FCSTD DOCUMENT  (FreeCAD 0.19R24366 (Git))
Label: hulltest3
License: All rights reserved
LicenseURL: http://en.wikipedia.org/wiki/All_rights_reserved
objects: Sketcher::SketchObject×2, PartDesign::Body×1
note: 3 computed .brp shape members not serialized (recipe doc carries the construction recipe); baked Part::Feature solids carry a one-line shape summary decoded from their .brp

FEATURE [Sketcher::SketchObject] Sketch  label="HullOutline"
  FullyConstrained = false
  Placement = pos=(0,0,0) rot=(0.980944,0.137386,0.137386;1.59004rad)
  Support = -> [XZ_Plane001]
  sketch-geometry (9):
    g0: LineSegment StartX=0 StartY=4e-16 StartZ=0 EndX=160 EndY=3 EndZ=0
    g1: LineSegment StartX=0 StartY=4e-16 StartZ=0 EndX=-20 EndY=70 EndZ=0
    g2: LineSegment StartX=-20 StartY=70 StartZ=0 EndX=-170 EndY=70 EndZ=0
    g3: LineSegment StartX=-170 StartY=70 StartZ=0 EndX=-190 EndY=194.294 EndZ=0
    g4: LineSegment StartX=-190 StartY=194.294 StartZ=0 EndX=420 EndY=194.294 EndZ=0
    g5: LineSegment StartX=420 StartY=194.294 StartZ=0 EndX=180 EndY=70 EndZ=0
    g6: LineSegment StartX=180 StartY=70 StartZ=0 EndX=160 EndY=3 EndZ=0
    g7: LineSegment StartX=-20 StartY=70 StartZ=0 EndX=180 EndY=70 EndZ=0
    g8: GeomPoint X=0 Y=194.294 Z=0
  constraints (23):
    c: Coincident(g1,g0)
    c: Horizontal(g2)
    c: Coincident(g3,g2)
    c: Horizontal(g4)
    c: Coincident(g6,g5)
    c: Coincident(g6,g0)
    c: DistanceX(g4,g4) = 610
    c: Coincident(g3,g4)
    c: DistanceX(g3,g2) = 20
    c: DistanceX(g2,g1) = 150
    c: Coincident(g2,g1)
    c: DistanceY(g0,g1) = 70
    c: DistanceX(g0,g0) = 160
    c: DistanceX(g1,g0) = 20
    c: DistanceY(g0,g0) = 3
    c: Horizontal(g1,g5)
    c: DistanceX(g0,g5) = 20
    c: Coincident(g5,g4)
    c: Coincident(g-1,g0)
    c: Coincident(g7,g1)
    c: Coincident(g7,g5)
    c: PointOnObject(g8,g4)
    c: PointOnObject(g8,g-2)
FEATURE [Sketcher::SketchObject] Sketch001
  ExternalGeometry = -> [Sketch,XZ_Plane001]
  FullyConstrained = false
  MapMode = 5
  Placement = pos=(0,0,0) rot=(0.57735,0.57735,0.57735;2.0944rad)
  Support = -> [YZ_Plane,Sketch]
  sketch-geometry (34):
    g0: Circle CenterX=112.53 CenterY=178.35 CenterZ=0 NormalX=0 NormalY=0 NormalZ=1 AngleXU=0 Radius=47.2198
    g1: LineSegment StartX=0 StartY=70 StartZ=0 EndX=20.3194 EndY=70 EndZ=0
    g2: LineSegment StartX=0 StartY=137.546 StartZ=0 EndX=136.295 EndY=137.546 EndZ=0
    g3: LineSegment StartX=0 StartY=209.52 StartZ=0 EndX=148 EndY=209.52 EndZ=0
    g4: LineSegment StartX=20.3194 StartY=70 StartZ=0 EndX=136.295 EndY=137.546 EndZ=0
    g5: LineSegment StartX=0 StartY=79.0612 StartZ=0 EndX=35.8772 EndY=79.0612 EndZ=0
    g6: LineSegment StartX=0 StartY=79.0612 StartZ=0 EndX=0 EndY=0 EndZ=0
    g7: LineSegment StartX=0 StartY=28.5019 StartZ=0 EndX=0 EndY=59.8573 EndZ=0
    g8: LineSegment StartX=0 StartY=209.52 StartZ=0 EndX=-148 EndY=209.52 EndZ=0
    g9: LineSegment StartX=0 StartY=185.529 StartZ=0 EndX=159.201 EndY=185.529 EndZ=0
    g10: LineSegment StartX=0 StartY=161.538 StartZ=0 EndX=156.655 EndY=161.538 EndZ=0
    g11: LineSegment StartX=0 StartY=120.734 StartZ=0 EndX=107.428 EndY=120.734 EndZ=0
    g12: LineSegment StartX=0 StartY=103.922 StartZ=0 EndX=78.562 EndY=103.922 EndZ=0
    g13: LineSegment StartX=0 StartY=209.52 StartZ=0 EndX=0 EndY=185.529 EndZ=0
    g14: LineSegment StartX=0 StartY=185.529 StartZ=0 EndX=0 EndY=161.538 EndZ=0
    g15: LineSegment StartX=0 StartY=137.546 StartZ=0 EndX=0 EndY=120.734 EndZ=0
    g16: LineSegment StartX=0 StartY=103.922 StartZ=0 EndX=0 EndY=120.734 EndZ=0
    g17: LineSegment StartX=0 StartY=103.922 StartZ=0 EndX=0 EndY=70 EndZ=0
    g18: LineSegment StartX=0 StartY=137.546 StartZ=0 EndX=0 EndY=161.538 EndZ=0
    g19: Circle CenterX=-112.53 CenterY=178.35 CenterZ=0 NormalX=0 NormalY=0 NormalZ=1 AngleXU=0 Radius=47.2198
    g20: LineSegment StartX=0 StartY=185.529 StartZ=0 EndX=-159.201 EndY=185.529 EndZ=0
    g21: LineSegment StartX=0 StartY=161.538 StartZ=0 EndX=-156.655 EndY=161.538 EndZ=0
    g22: LineSegment StartX=0 StartY=137.546 StartZ=0 EndX=-136.295 EndY=137.546 EndZ=0
    g23: LineSegment StartX=0 StartY=120.734 StartZ=0 EndX=-107.428 EndY=120.734 EndZ=0
    g24: LineSegment StartX=0 StartY=103.922 StartZ=0 EndX=-78.562 EndY=103.922 EndZ=0
    g25: LineSegment StartX=0 StartY=70 StartZ=0 EndX=-20.3194 EndY=70 EndZ=0
    g26: LineSegment StartX=-20.3194 StartY=70 StartZ=0 EndX=-78.562 EndY=103.922 EndZ=0
    g27: LineSegment StartX=-78.562 StartY=103.922 StartZ=0 EndX=-107.428 EndY=120.734 EndZ=0
    g28: LineSegment StartX=-107.428 StartY=120.734 StartZ=0 EndX=-136.295 EndY=137.546 EndZ=0
    g29: LineSegment StartX=0 StartY=79.0612 StartZ=0 EndX=-35.8772 EndY=79.0612 EndZ=0
    g30: LineSegment StartX=-20.3194 StartY=70 StartZ=0 EndX=-20.3194 EndY=0 EndZ=0
    g31: LineSegment StartX=-20.3194 StartY=0 StartZ=0 EndX=0 EndY=0 EndZ=0
    g32: LineSegment StartX=0 StartY=0 StartZ=0 EndX=20.3194 EndY=0 EndZ=0
    g33: LineSegment StartX=20.3194 StartY=0 StartZ=0 EndX=20.3194 EndY=70 EndZ=0
  constraints (93):
    c: Horizontal(g1)
    c: PointOnObject(g2,g-2)
    c: Horizontal(g2)
    c: PointOnObject(g3,g-2)
    c: Horizontal(g3)
    c: PointOnObject(g2,g0)
    c: PointOnObject(g3,g0)
    c: Coincident(g4,g1)
    c: PointOnObject(g4,g0)
    c: Tangent(g0,g4)
    c: PointOnObject(g5,g4)
    c: Horizontal(g5)
    c: Coincident(g6,g5)
    c: Vertical(g7)
    c: Coincident(g8,g3)
    c: Horizontal(g8)
    c: DistanceX(g8,g3) = 296
    c: Vertical(g6)
    c: DistanceY(g6,g1) = 70
    c: PointOnObject(g9,g0)
    c: Horizontal(g9)
    c: PointOnObject(g10,g0)
    c: Horizontal(g10)
    c: PointOnObject(g11,g4)
    c: Horizontal(g11)
    c: PointOnObject(g12,g4)
    c: Horizontal(g12)
    c: Coincident(g13,g3)
    c: Coincident(g13,g9)
    c: Vertical(g13)
    c: Coincident(g14,g9)
    c: Coincident(g14,g10)
    c: Vertical(g14)
    c: Coincident(g15,g2)
    c: Coincident(g15,g11)
    c: Vertical(g15)
    c: Coincident(g16,g12)
    c: Coincident(g16,g11)
    c: Vertical(g16)
    c: Coincident(g17,g12)
    c: Coincident(g17,g1)
    c: Vertical(g17)
    c: Equal(g16,g15)
    c: Coincident(g18,g2)
    c: Coincident(g18,g10)
    c: Equal(g18,g14)
    c: Equal(g14,g13)
    c: DistanceY(g17,g3) = 139.52
    c: PointOnObject(g8,g19)
    c: Coincident(g20,g9)
    c: PointOnObject(g20,g19)
    c: Horizontal(g20)
    c: Coincident(g21,g10)
    c: PointOnObject(g21,g19)
    c: Horizontal(g21)
    c: Coincident(g22,g2)
    c: PointOnObject(g22,g19)
    c: Coincident(g23,g11)
    c: Horizontal(g23)
    c: Coincident(g24,g12)
    c: Horizontal(g24)
    c: Coincident(g25,g17)
    c: Horizontal(g25)
    c: Coincident(g26,g25)
    c: Coincident(g26,g24)
    c: Coincident(g27,g24)
    c: Coincident(g27,g23)
    c: Coincident(g28,g22)
    c: Equal(g11,g23)
    c: Coincident(g28,g23)
    c: Horizontal(g22)
    c: Equal(g2,g22)
    c: Horizontal(g0,g19)
    c: Equal(g9,g20)
    c: Equal(g24,g12)
    c: Equal(g25,g1)
    c: PointOnObject(g5,g7)
    c: PointOnObject(g7,g17)
    c: Coincident(g29,g5)
    c: PointOnObject(g29,g26)
    c: Horizontal(g29)
    c: Coincident(g30,g25)
    c: Vertical(g30)
    c: Coincident(g31,g6)
    c: Horizontal(g31)
    c: Coincident(g32,g6)
    c: Horizontal(g32)
    c: Coincident(g33,g32)
    c: Coincident(g33,g1)
    c: Vertical(g33)
    c: Horizontal(g-1,g6)
    c: Coincident(g30,g31)
    c: Tangent(g28,g19)
FEATURE [PartDesign::Body] Body
  Group = -> [Sketch001,Sketch]
  Origin = -> Origin
